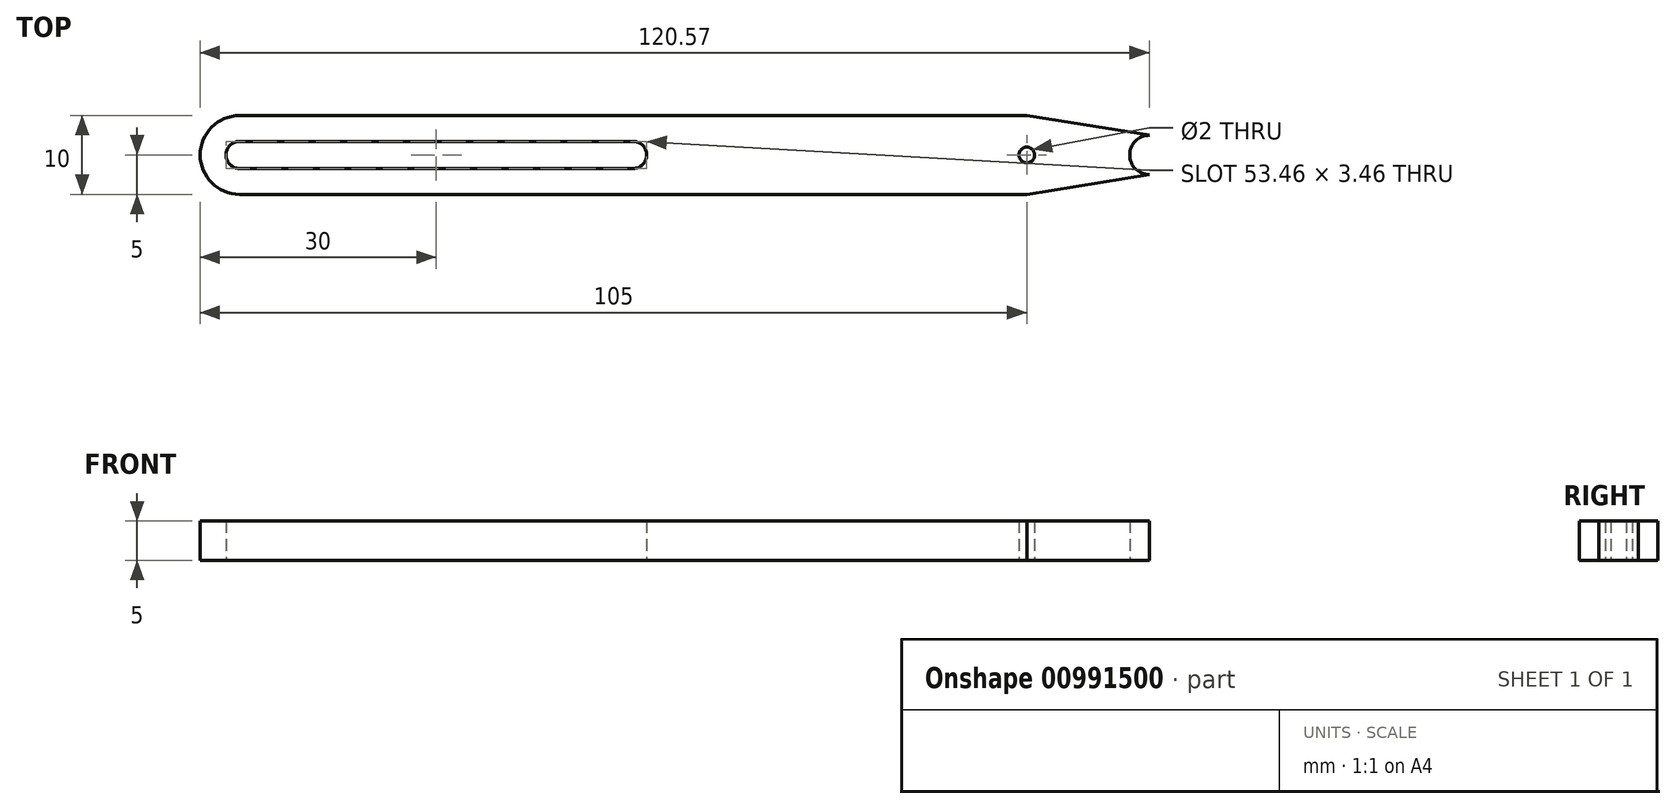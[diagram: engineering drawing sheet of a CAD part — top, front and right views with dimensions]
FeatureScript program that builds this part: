
annotation { "Feature Type Name" : "Feature", "Feature Type Description" : "" }
export const myFeature = defineFeature(function(context is Context, id is Id, definition is map)
    precondition{}
    {
        {
            var Q0;
            Q0=qCreatedBy(makeId("Top.planeOp"),FACE);
            var sketch = newSketch(context, id + "F0", { "sketchPlane" : qUnion([Q0])});
            skLineSegment(sketch, "E0.bottom", {"start": v(50, 5) * mm, "end": v(-50, 5) * mm});
            skLineSegment(sketch, "E0.top", {"start": v(50, -5) * mm, "end": v(-50, -5) * mm});
            skLineSegment(sketch, "E0.left", {"start": v(50, 5) * mm, "end": v(50, -5) * mm, "construction": true});
            skLineSegment(sketch, "E0.right", {"start": v(-50, 5) * mm, "end": v(-50, -5) * mm, "construction": true});
            skPoint(sketch, "E0.middle", {"position": v(0, 0) * mm});
            skArc(sketch, "E1", {"start": v(-50, 5) * mm, "mid": v(-55, 0) * mm, "end": v(-50, -5) * mm});
            skArc(sketch, "E2", {"start": v(65.57, 2.5) * mm, "mid": v(63.07, 0) * mm, "end": v(65.57, -2.5) * mm});
            skLineSegment(sketch, "E3", {"start": v(65.57, 2.5) * mm, "end": v(50, 5) * mm});
            skLineSegment(sketch, "E4", {"start": v(65.57, -2.5) * mm, "end": v(50, -5) * mm});
            skLineSegment(sketch, "E5", {"start": v(65.57, 34.92) * mm, "end": v(65.57, -39.92) * mm, "construction": true});
            skArc(sketch, "E6", {"start": v(-50, 1.73) * mm, "mid": v(-51.73, 0) * mm, "end": v(-50, -1.73) * mm});
            skArc(sketch, "E7", {"start": v(0, -1.73) * mm, "mid": v(1.73, 0) * mm, "end": v(0, 1.73) * mm});
            skLineSegment(sketch, "E8", {"start": v(-50, 1.73) * mm, "end": v(0, 1.73) * mm});
            skLineSegment(sketch, "E9", {"start": v(0, -1.73) * mm, "end": v(-50, -1.73) * mm});
            skLineSegment(sketch, "E10", {"start": v(-50, -1.73) * mm, "end": v(-50, 1.73) * mm, "construction": true});
            skCircle(sketch, "E11", {"center": v(50, 0) * mm, "radius": 1 * mm});
            skSolve(sketch);
        }
        {
            var Q0;
            Q0=makeQuery(id+"F0.imprint","IMPRINT",FACE,{"disambiguationData":[TD([[makeQuery(id+"F0.imprint","IMPRINT",EDGE,{"derivedFrom":sQuery(id+"F0.wireOp",EDGE,"E0.bottom")}),1.0]])]});
            extrude(context, id + "F1", {"entities" : qUnion([Q0]), "depth" : 5 * mm, "offsetDistance" : 25 * mm});
        }
    });
